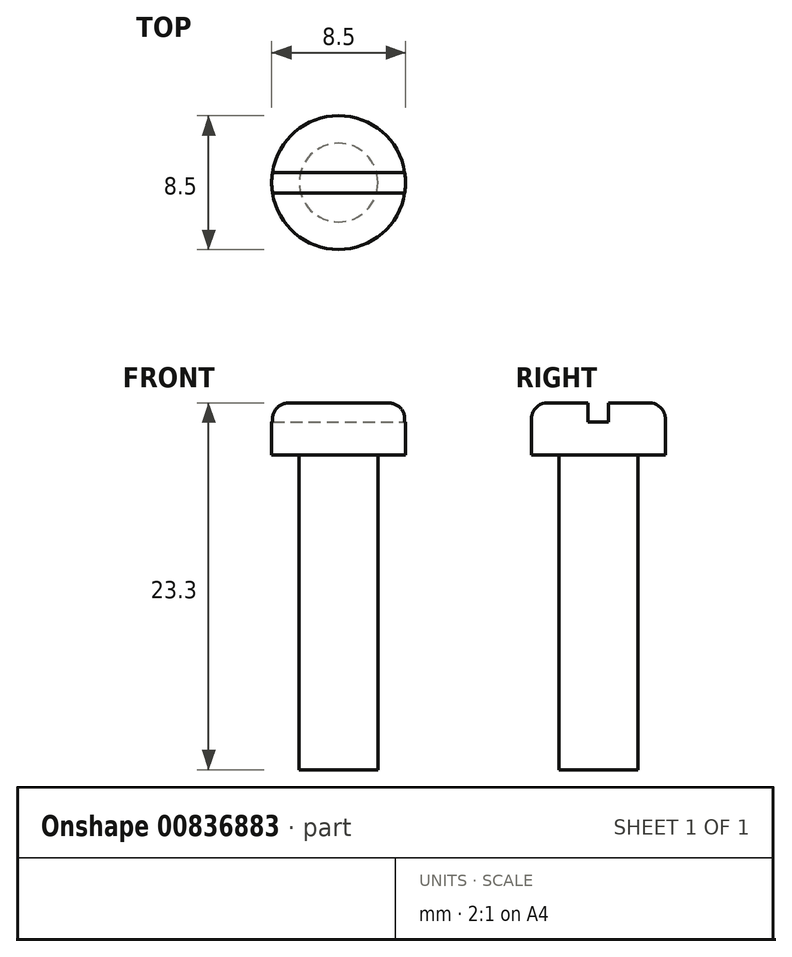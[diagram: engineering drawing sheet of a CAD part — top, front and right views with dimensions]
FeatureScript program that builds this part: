
annotation { "Feature Type Name" : "Feature", "Feature Type Description" : "" }
export const myFeature = defineFeature(function(context is Context, id is Id, definition is map)
    precondition{}
    {
        {
            var Q0;
            Q0=qCreatedBy(makeId("Top.planeOp"),FACE);
            var sketch = newSketch(context, id + "F0", { "sketchPlane" : qUnion([Q0])});
            skPoint(sketch, "E0.0.midPoint", {"position": v(0, 3.68) * mm});
            skCircle(sketch, "E1", {"center": v(0, 0) * mm, "radius": 4.25 * mm});
            skPoint(sketch, "E0.0.end.orphan", {"position": v(2.12, 3.68) * mm});
            skPoint(sketch, "E0.5.end.orphan", {"position": v(-2.12, 3.68) * mm});
            skSolve(sketch);
        }
        {
            var Q0;
            Q0 = qSketchRegion(id + "F0", true);
            extrude(context, id + "F1", {"entities" : qUnion([Q0]), "depth" : 3.3 * mm, "offsetDistance" : 25.4 * mm});
        }
        {
            var Q0;
            Q0=makeQuery(id+"F1.opExtrude","CAP_FACE",FACE,{"disambiguationData":[OSD([sQuery(id+"F0.wireOp",EDGE,"E1")])],"isStart":true});
            var sketch = newSketch(context, id + "F2", { "sketchPlane" : qUnion([Q0])});
            skCircle(sketch, "E2", {"center": v(0, 0) * mm, "radius": 2.5 * mm});
            skSolve(sketch);
        }
        {
            var Q0;
            Q0 = qSketchRegion(id + "F2", true);
            extrude(context, id + "F3", {"entities" : qUnion([Q0]), "operationType" : NewBodyOperationType.ADD, "depth" : 20 * mm, "offsetDistance" : 25.4 * mm});
        }
        {
            var Q0;
            Q0=makeQuery(id+"F1.opExtrude","CAP_FACE",FACE,{"disambiguationData":[OSD([sQuery(id+"F0.wireOp",EDGE,"E1")])],"isStart":false});
            var sketch = newSketch(context, id + "F4", { "sketchPlane" : qUnion([Q0])});
            skLineSegment(sketch, "E3.bottom", {"start": v(-6.1, -0.65) * mm, "end": v(6.1, -0.65) * mm});
            skLineSegment(sketch, "E3.top", {"start": v(-6.1, 0.65) * mm, "end": v(6.1, 0.65) * mm});
            skLineSegment(sketch, "E3.left", {"start": v(-6.1, -0.65) * mm, "end": v(-6.1, 0.65) * mm});
            skLineSegment(sketch, "E3.right", {"start": v(6.1, -0.65) * mm, "end": v(6.1, 0.65) * mm});
            skPoint(sketch, "E3.middle", {"position": v(0, 0) * mm});
            skSolve(sketch);
        }
        {
            var Q0;
            Q0 = qSketchRegion(id + "F4", true);
            extrude(context, id + "F5", {"entities" : qUnion([Q0]), "operationType" : NewBodyOperationType.REMOVE, "oppositeDirection" : true, "depth" : 1.2 * mm, "offsetDistance" : 25.4 * mm});
        }
        {
            var Q0;
            {var subQ0=sQuery(id+"F0.wireOp",EDGE,"E1");Q0=makeQuery(id+"F5.boolean.opBoolean","SPLIT",EDGE,{"disambiguationData":[TD([makeQuery(id+"F5.opExtrude","SWEPT_FACE",FACE,{"disambiguationData":[OSD([sQuery(id+"F4.wireOp",EDGE,"E3.top")])]})])],"derivedFrom":makeQuery(id+"F1.opExtrude","CAP_EDGE",EDGE,{"disambiguationData":[OSD([subQ0])],"isStart":false})});}
            var Q1;
            {var subQ0=sQuery(id+"F0.wireOp",EDGE,"E1");Q1=makeQuery(id+"F5.boolean.opBoolean","SPLIT",EDGE,{"disambiguationData":[TD([makeQuery(id+"F5.opExtrude","SWEPT_FACE",FACE,{"disambiguationData":[OSD([sQuery(id+"F4.wireOp",EDGE,"E3.bottom")])]})])],"derivedFrom":makeQuery(id+"F1.opExtrude","CAP_EDGE",EDGE,{"disambiguationData":[OSD([subQ0])],"isStart":false})});}
            fillet(context, id + "F6", {"entities" : qUnion([Q0, Q1]), "radius" : 1 * mm, "tangentPropagation" : true, "allowEdgeOverflow" : false});
        }
    });
